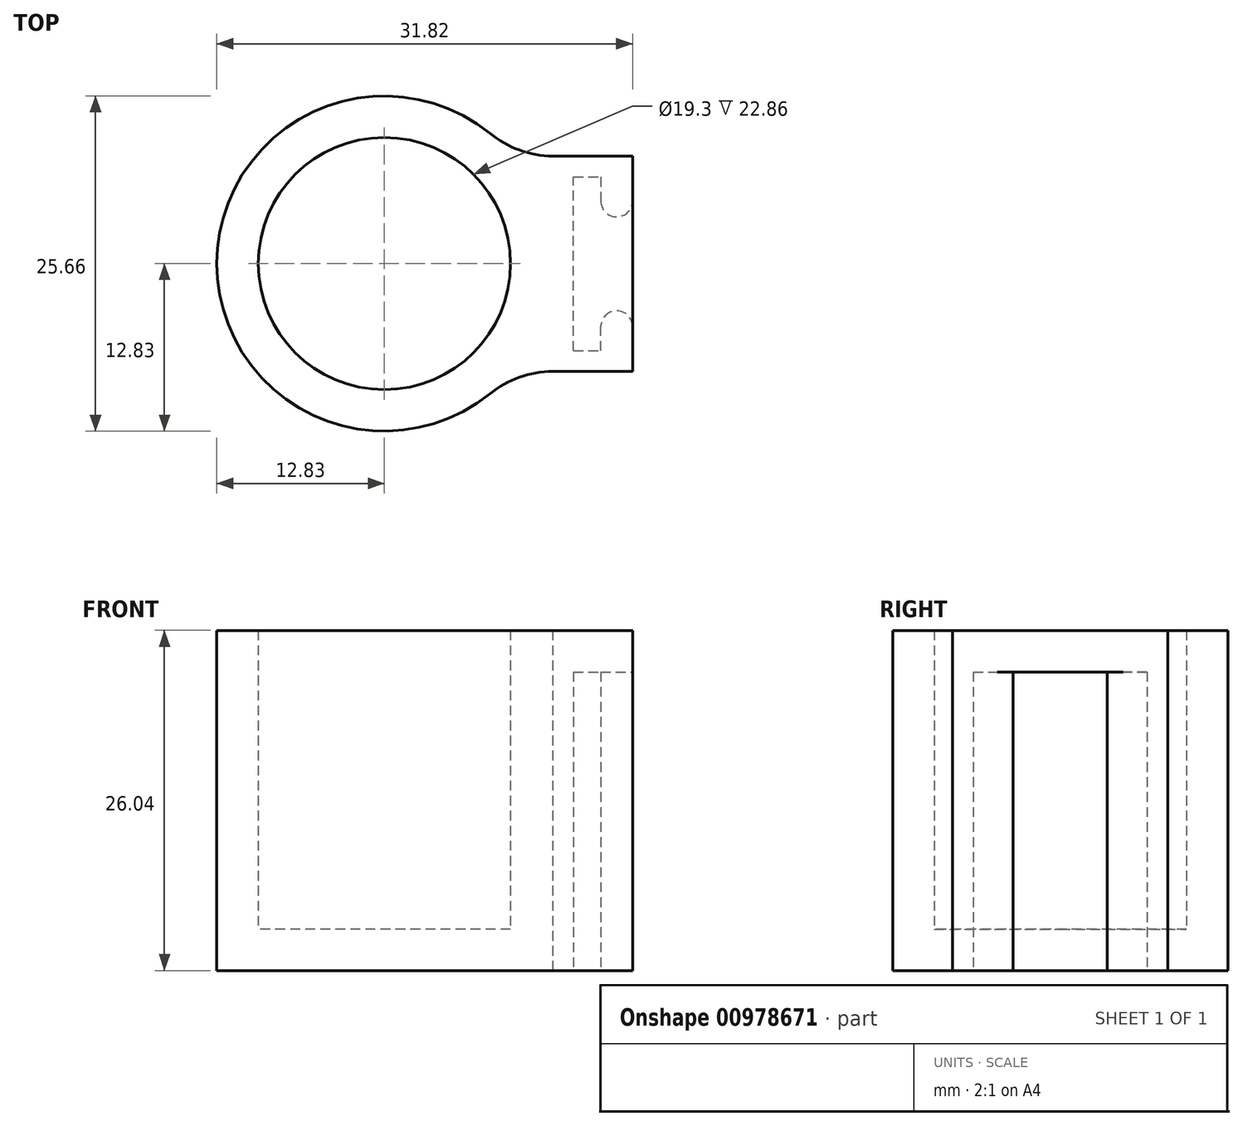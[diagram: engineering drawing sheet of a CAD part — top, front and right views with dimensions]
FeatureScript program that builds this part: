
annotation { "Feature Type Name" : "Feature", "Feature Type Description" : "" }
export const myFeature = defineFeature(function(context is Context, id is Id, definition is map)
    precondition{}
    {
        {
            var Q0;
            Q0=qCreatedBy(makeId("Top.planeOp"),FACE);
            var sketch = newSketch(context, id + "F0", { "sketchPlane" : qUnion([Q0])});
            skLineSegment(sketch, "E0", {"start": v(14.73, -0.02) * mm, "end": v(34.4, -0.02) * mm, "construction": true});
            skLineSegment(sketch, "E1", {"start": v(16.19, -6.42) * mm, "end": v(16.19, -4.83) * mm, "construction": true});
            skLineSegment(sketch, "E2", {"start": v(17.76, -3.25) * mm, "end": v(17.77, -3.25) * mm, "construction": true});
            skLineSegment(sketch, "E3", {"start": v(19.36, -4.85) * mm, "end": v(19.36, -6.42) * mm, "construction": true});
            skPoint(sketch, "E4.visualSharp", {"position": v(16.19, -3.25) * mm});
            skArc(sketch, "E4.filletArc", {"start": v(17.77, -3.25) * mm, "mid": v(16.65, -3.71) * mm, "end": v(16.19, -4.83) * mm, "construction": true});
            skPoint(sketch, "E5.visualSharp", {"position": v(19.36, -3.25) * mm});
            skArc(sketch, "E5.filletArc", {"start": v(19.36, -4.85) * mm, "mid": v(18.9, -3.72) * mm, "end": v(17.76, -3.25) * mm, "construction": true});
            skLineSegment(sketch, "E6.MirrorCS", {"start": v(17.76, 3.2) * mm, "end": v(17.77, 3.2) * mm, "construction": true});
            skPoint(sketch, "E7.MirrorP", {"position": v(16.19, 3.2) * mm});
            skArc(sketch, "E8.MirrorCS", {"start": v(19.36, 4.8) * mm, "mid": v(18.9, 3.67) * mm, "end": v(17.76, 3.2) * mm, "construction": true});
            skLineSegment(sketch, "E9.MirrorCS", {"start": v(16.19, 6.38) * mm, "end": v(16.19, 4.8) * mm, "construction": true});
            skArc(sketch, "E10.MirrorCS", {"start": v(17.77, 3.2) * mm, "mid": v(16.65, 3.67) * mm, "end": v(16.19, 4.8) * mm, "construction": true});
            skLineSegment(sketch, "E11.MirrorCS", {"start": v(19.36, 4.8) * mm, "end": v(19.36, 6.38) * mm, "construction": true});
            skPoint(sketch, "E12.MirrorP", {"position": v(19.36, 3.2) * mm});
            skPoint(sketch, "E13.orphan", {"position": v(17.77, -6.42) * mm});
            skLineSegment(sketch, "E14.0", {"start": v(14.73, 6.38) * mm, "end": v(16.19, 6.38) * mm, "construction": true});
            skLineSegment(sketch, "E14.1", {"start": v(14.73, 6.38) * mm, "end": v(14.73, -6.42) * mm, "construction": true});
            skLineSegment(sketch, "E15.MirrorCS", {"start": v(14.73, -6.42) * mm, "end": v(16.19, -6.42) * mm, "construction": true});
            skPoint(sketch, "E16.orphan", {"position": v(17.77, 6.38) * mm});
            skLineSegment(sketch, "E17.0", {"start": v(14.47, 6.28) * mm, "end": v(14.47, -6.42) * mm});
            skLineSegment(sketch, "E18.0", {"start": v(14.6, 6.63) * mm, "end": v(16.19, 6.63) * mm});
            skLineSegment(sketch, "E19", {"start": v(16.19, 6.63) * mm, "end": v(16.56, 6.63) * mm});
            skLineSegment(sketch, "E20", {"start": v(16.56, 6.63) * mm, "end": v(16.56, 4.8) * mm});
            skLineSegment(sketch, "E21", {"start": v(17.77, 7.48) * mm, "end": v(17.77, 2.52) * mm, "construction": true});
            skLineSegment(sketch, "E22.MirrorCS", {"start": v(19, 6.63) * mm, "end": v(19, 4.8) * mm});
            skArc(sketch, "E23", {"start": v(16.56, 4.8) * mm, "mid": v(17.77, 3.58) * mm, "end": v(19, 4.8) * mm});
            skLineSegment(sketch, "E24.MirrorCS", {"start": v(19, -6.68) * mm, "end": v(19, -4.83) * mm});
            skLineSegment(sketch, "E25.MirrorCS", {"start": v(16.56, -6.68) * mm, "end": v(16.56, -4.83) * mm});
            skLineSegment(sketch, "E26.MirrorCS", {"start": v(16.19, -6.68) * mm, "end": v(16.56, -6.68) * mm});
            skArc(sketch, "E27.MirrorCS", {"start": v(16.56, -4.83) * mm, "mid": v(17.77, -3.62) * mm, "end": v(19, -4.83) * mm});
            skLineSegment(sketch, "E28", {"start": v(16.19, -6.68) * mm, "end": v(14.47, -6.68) * mm});
            skLineSegment(sketch, "E29", {"start": v(14.47, -6.68) * mm, "end": v(14.47, -6.42) * mm});
            skLineSegment(sketch, "E30", {"start": v(14.47, 6.28) * mm, "end": v(14.47, 6.63) * mm});
            skLineSegment(sketch, "E31", {"start": v(14.47, 6.63) * mm, "end": v(14.6, 6.63) * mm});
            skLineSegment(sketch, "E32", {"start": v(19, 6.63) * mm, "end": v(19, 8.22) * mm});
            skLineSegment(sketch, "E33", {"start": v(19, 8.22) * mm, "end": v(14.47, 8.22) * mm});
            skLineSegment(sketch, "E34", {"start": v(14.47, 8.22) * mm, "end": v(12.88, 8.22) * mm});
            skLineSegment(sketch, "E35.bottom", {"start": v(-37.03, 11.9) * mm, "end": v(-37.03, 11.9) * mm});
            skLineSegment(sketch, "E35.top", {"start": v(-37.03, -4.39) * mm, "end": v(-37.03, -4.39) * mm});
            skLineSegment(sketch, "E36.MirrorCS", {"start": v(19, -8.26) * mm, "end": v(14.47, -8.26) * mm});
            skLineSegment(sketch, "E37.MirrorCS", {"start": v(14.47, -8.26) * mm, "end": v(12.88, -8.26) * mm});
            skPoint(sketch, "E38.orphan", {"position": v(12.88, -8.26) * mm});
            skLineSegment(sketch, "E39", {"start": v(19, -8.26) * mm, "end": v(19, -6.68) * mm});
            skLineSegment(sketch, "E40", {"start": v(9.65, 0) * mm, "end": v(12.83, 0) * mm, "construction": true});
            skLineSegment(sketch, "E41", {"start": v(9.65, 0) * mm, "end": v(-9.65, 0) * mm, "construction": true});
            skCircle(sketch, "E42", {"center": v(0, 0) * mm, "radius": 9.65 * mm});
            skArc(sketch, "E43.0", {"start": v(8.07, 9.97) * mm, "mid": v(-12.83, 0) * mm, "end": v(8.07, -9.97) * mm});
            skArc(sketch, "E44", {"start": v(8.07, 9.97) * mm, "mid": v(10.33, 8.7) * mm, "end": v(12.88, 8.22) * mm});
            skArc(sketch, "E45", {"start": v(12.88, -8.26) * mm, "mid": v(10.33, -8.7) * mm, "end": v(8.07, -9.97) * mm});
            skSolve(sketch);
        }
        {
            var Q0;
            Q0=makeQuery(id+"F0.imprint","IMPRINT",FACE,{"disambiguationData":[TD([[makeQuery(id+"F0.imprint","IMPRINT",EDGE,{"derivedFrom":sQuery(id+"F0.wireOp",EDGE,"E17.0")}),-1.0]])]});
            extrude(context, id + "F1", {"entities" : qUnion([Q0]), "depth" : 22.86 * mm, "offsetDistance" : 25.4 * mm});
        }
        {
            var Q0;
            Q0=makeQuery(id+"F1.opExtrude","CAP_FACE",FACE,{"disambiguationData":[OSD([sQuery(id+"F0.wireOp",EDGE,"E17.0"),sQuery(id+"F0.wireOp",EDGE,"E18.0"),sQuery(id+"F0.wireOp",EDGE,"E19"),sQuery(id+"F0.wireOp",EDGE,"E20"),sQuery(id+"F0.wireOp",EDGE,"E22.MirrorCS"),sQuery(id+"F0.wireOp",EDGE,"E23"),sQuery(id+"F0.wireOp",EDGE,"E24.MirrorCS"),sQuery(id+"F0.wireOp",EDGE,"E25.MirrorCS"),sQuery(id+"F0.wireOp",EDGE,"E26.MirrorCS"),sQuery(id+"F0.wireOp",EDGE,"E27.MirrorCS"),sQuery(id+"F0.wireOp",EDGE,"E28"),sQuery(id+"F0.wireOp",EDGE,"E29"),sQuery(id+"F0.wireOp",EDGE,"E30"),sQuery(id+"F0.wireOp",EDGE,"E31"),sQuery(id+"F0.wireOp",EDGE,"E32"),sQuery(id+"F0.wireOp",EDGE,"E33"),sQuery(id+"F0.wireOp",EDGE,"E34"),sQuery(id+"F0.wireOp",EDGE,"E36.MirrorCS"),sQuery(id+"F0.wireOp",EDGE,"E37.MirrorCS"),sQuery(id+"F0.wireOp",EDGE,"E39"),sQuery(id+"F0.wireOp",EDGE,"E42"),sQuery(id+"F0.wireOp",EDGE,"E43.0"),sQuery(id+"F0.wireOp",EDGE,"E44"),sQuery(id+"F0.wireOp",EDGE,"E45")])],"isStart":false});
            var sketch = newSketch(context, id + "F2", { "sketchPlane" : qUnion([Q0])});
            skArc(sketch, "E46.0", {"start": v(8.07, 9.97) * mm, "mid": v(-12.83, 0) * mm, "end": v(8.07, -9.97) * mm});
            skArc(sketch, "E47.0", {"start": v(8.07, 9.97) * mm, "mid": v(10.33, 8.7) * mm, "end": v(12.88, 8.22) * mm});
            skLineSegment(sketch, "E48.0", {"start": v(19, 8.22) * mm, "end": v(12.88, 8.22) * mm});
            skLineSegment(sketch, "E49.0", {"start": v(19, -8.26) * mm, "end": v(12.88, -8.26) * mm});
            skArc(sketch, "E50.0", {"start": v(12.88, -8.26) * mm, "mid": v(10.33, -8.7) * mm, "end": v(8.07, -9.97) * mm});
            skCircle(sketch, "E51.0", {"center": v(0, 0) * mm, "radius": 9.65 * mm});
            skLineSegment(sketch, "E52", {"start": v(19, 8.22) * mm, "end": v(19, -8.26) * mm});
            skSolve(sketch);
        }
        {
            var Q0;
            Q0=makeQuery(id+"F2.imprint","IMPRINT",FACE,{"disambiguationData":[TD([[makeQuery(id+"F2.imprint","IMPRINT",EDGE,{"derivedFrom":sQuery(id+"F2.wireOp",EDGE,"E46.0")}),1.0]])]});
            var Q1;
            Q1=makeQuery(id+"F2.imprint","IMPRINT",FACE,{"disambiguationData":[TD([[makeQuery(id+"F2.imprint","IMPRINT",EDGE,{"derivedFrom":makeQuery(id+"F1.opExtrude","CAP_EDGE",EDGE,{"disambiguationData":[OSD([sQuery(id+"F0.wireOp",EDGE,"E20")])],"isStart":false})}),-1.0]])]});
            extrude(context, id + "F3", {"entities" : qUnion([Q0, Q1]), "operationType" : NewBodyOperationType.ADD, "depth" : 3.17 * mm, "offsetDistance" : 25.4 * mm});
        }
        {
            var Q0;
            Q0=makeQuery(id+"F1.opExtrude","CAP_FACE",FACE,{"disambiguationData":[OSD([sQuery(id+"F0.wireOp",EDGE,"E17.0"),sQuery(id+"F0.wireOp",EDGE,"E18.0"),sQuery(id+"F0.wireOp",EDGE,"E19"),sQuery(id+"F0.wireOp",EDGE,"E20"),sQuery(id+"F0.wireOp",EDGE,"E22.MirrorCS"),sQuery(id+"F0.wireOp",EDGE,"E23"),sQuery(id+"F0.wireOp",EDGE,"E24.MirrorCS"),sQuery(id+"F0.wireOp",EDGE,"E25.MirrorCS"),sQuery(id+"F0.wireOp",EDGE,"E26.MirrorCS"),sQuery(id+"F0.wireOp",EDGE,"E27.MirrorCS"),sQuery(id+"F0.wireOp",EDGE,"E28"),sQuery(id+"F0.wireOp",EDGE,"E29"),sQuery(id+"F0.wireOp",EDGE,"E30"),sQuery(id+"F0.wireOp",EDGE,"E31"),sQuery(id+"F0.wireOp",EDGE,"E32"),sQuery(id+"F0.wireOp",EDGE,"E33"),sQuery(id+"F0.wireOp",EDGE,"E34"),sQuery(id+"F0.wireOp",EDGE,"E36.MirrorCS"),sQuery(id+"F0.wireOp",EDGE,"E37.MirrorCS"),sQuery(id+"F0.wireOp",EDGE,"E39"),sQuery(id+"F0.wireOp",EDGE,"E42"),sQuery(id+"F0.wireOp",EDGE,"E43.0"),sQuery(id+"F0.wireOp",EDGE,"E44"),sQuery(id+"F0.wireOp",EDGE,"E45")])],"isStart":true});
            var sketch = newSketch(context, id + "F4", { "sketchPlane" : qUnion([Q0])});
            skCircle(sketch, "E53.0", {"center": v(0, 0) * mm, "radius": 9.65 * mm});
            skSolve(sketch);
        }
        {
            var Q0;
            Q0=makeQuery(id+"F4.imprint","IMPRINT",FACE,{"disambiguationData":[TD([[makeQuery(id+"F4.imprint","IMPRINT",EDGE,{"derivedFrom":sQuery(id+"F4.wireOp",EDGE,"E53.0")}),-1.0]])]});
            extrude(context, id + "F5", {"entities" : qUnion([Q0]), "operationType" : NewBodyOperationType.ADD, "oppositeDirection" : true, "depth" : 3.17 * mm, "offsetDistance" : 25.4 * mm});
        }
    });
